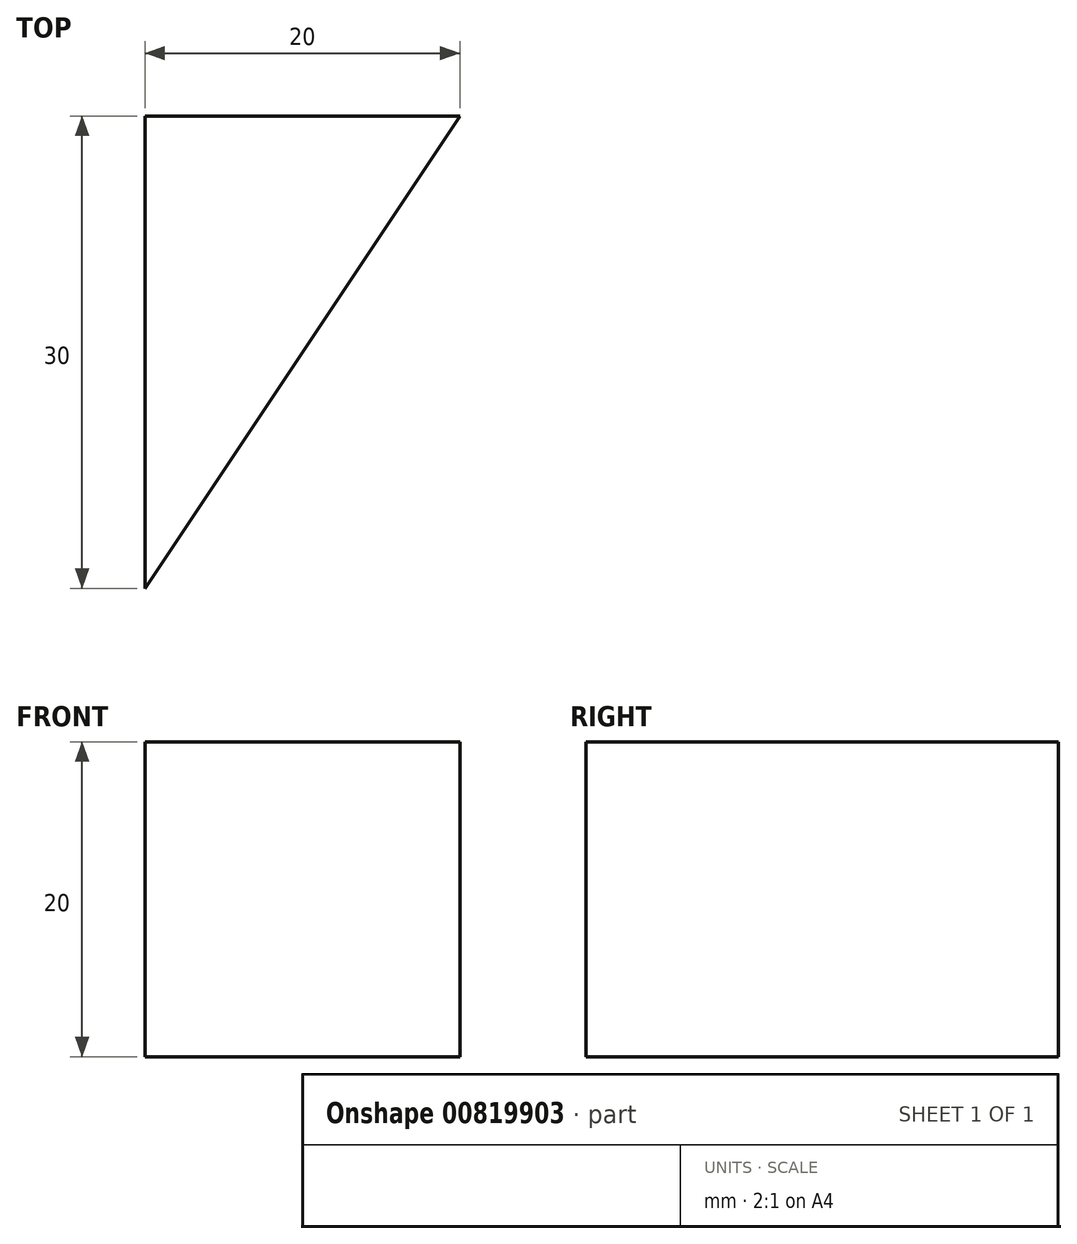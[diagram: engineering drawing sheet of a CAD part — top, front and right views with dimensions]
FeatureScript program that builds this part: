
annotation { "Feature Type Name" : "Feature", "Feature Type Description" : "" }
export const myFeature = defineFeature(function(context is Context, id is Id, definition is map)
    precondition{}
    {
        {
            var Q0;
            Q0=qCreatedBy(makeId("Top.planeOp"),FACE);
            var sketch = newSketch(context, id + "F0", { "sketchPlane" : qUnion([Q0])});
            skLineSegment(sketch, "E0.bottom", {"start": v(0, 0) * mm, "end": v(50, 0) * mm});
            skLineSegment(sketch, "E0.top", {"start": v(0, -150) * mm, "end": v(50, -150) * mm});
            skLineSegment(sketch, "E0.left", {"start": v(0, 0) * mm, "end": v(0, -150) * mm});
            skLineSegment(sketch, "E0.right", {"start": v(50, 0) * mm, "end": v(50, -150) * mm});
            skLineSegment(sketch, "E1", {"start": v(0, 0) * mm, "end": v(20, 0) * mm});
            skLineSegment(sketch, "E2", {"start": v(0, 0) * mm, "end": v(0, -30) * mm});
            skLineSegment(sketch, "E3", {"start": v(20, 0) * mm, "end": v(0, -30) * mm});
            skSolve(sketch);
        }
        {
            var Q0;
            Q0=makeQuery(id+"F0.imprint","IMPRINT",FACE,{"disambiguationData":[TD([[makeQuery(id+"F0.imprint","IMPRINT",EDGE,{"derivedFrom":sQuery(id+"F0.wireOp",EDGE,"E0.bottom")}),-1.0]])]});
            extrude(context, id + "F1", {"entities" : qUnion([Q0]), "depth" : 20 * mm, "offsetDistance" : 25 * mm});
        }
    });
